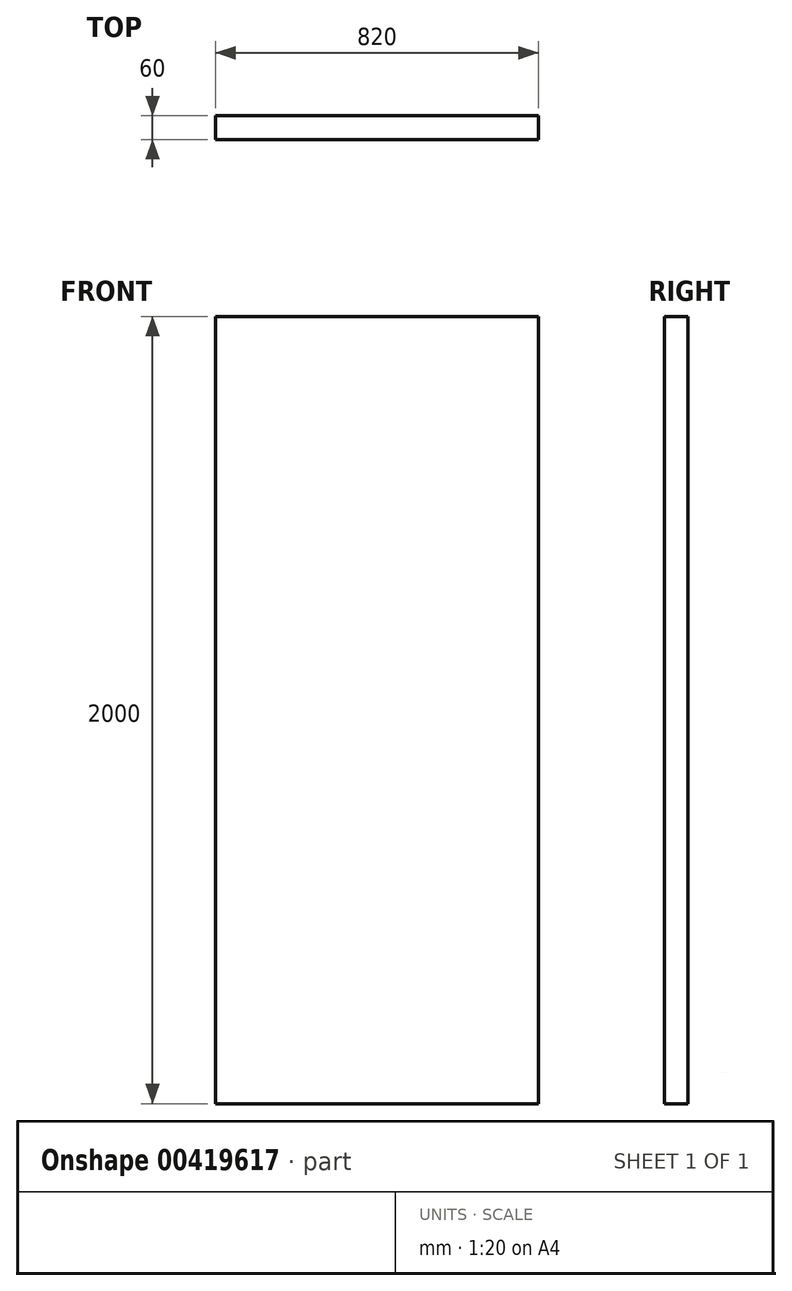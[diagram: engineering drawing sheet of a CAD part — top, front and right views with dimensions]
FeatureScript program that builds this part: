
annotation { "Feature Type Name" : "Feature", "Feature Type Description" : "" }
export const myFeature = defineFeature(function(context is Context, id is Id, definition is map)
    precondition{}
    {
        {
            var Q0;
            Q0=qCreatedBy(makeId("Top.planeOp"),FACE);
            var sketch = newSketch(context, id + "F0", { "sketchPlane" : qUnion([Q0])});
            skLineSegment(sketch, "E0.bottom", {"start": v(-696.28, 49.75) * mm, "end": v(123.72, 49.75) * mm});
            skLineSegment(sketch, "E0.top", {"start": v(-696.28, -10.25) * mm, "end": v(123.72, -10.25) * mm});
            skLineSegment(sketch, "E0.left", {"start": v(-696.28, 49.75) * mm, "end": v(-696.28, -10.25) * mm});
            skLineSegment(sketch, "E0.right", {"start": v(123.72, 49.75) * mm, "end": v(123.72, -10.25) * mm});
            skSolve(sketch);
        }
        {
            var Q0;
            Q0=makeQuery(id+"F0.imprint","IMPRINT",FACE,{"disambiguationData":[TD([[makeQuery(id+"F0.imprint","IMPRINT",EDGE,{"derivedFrom":sQuery(id+"F0.wireOp",EDGE,"E0.bottom")}),-1.0]])]});
            extrude(context, id + "F1", {"entities" : qUnion([Q0]), "depth" : 2000 * mm});
        }
    });
